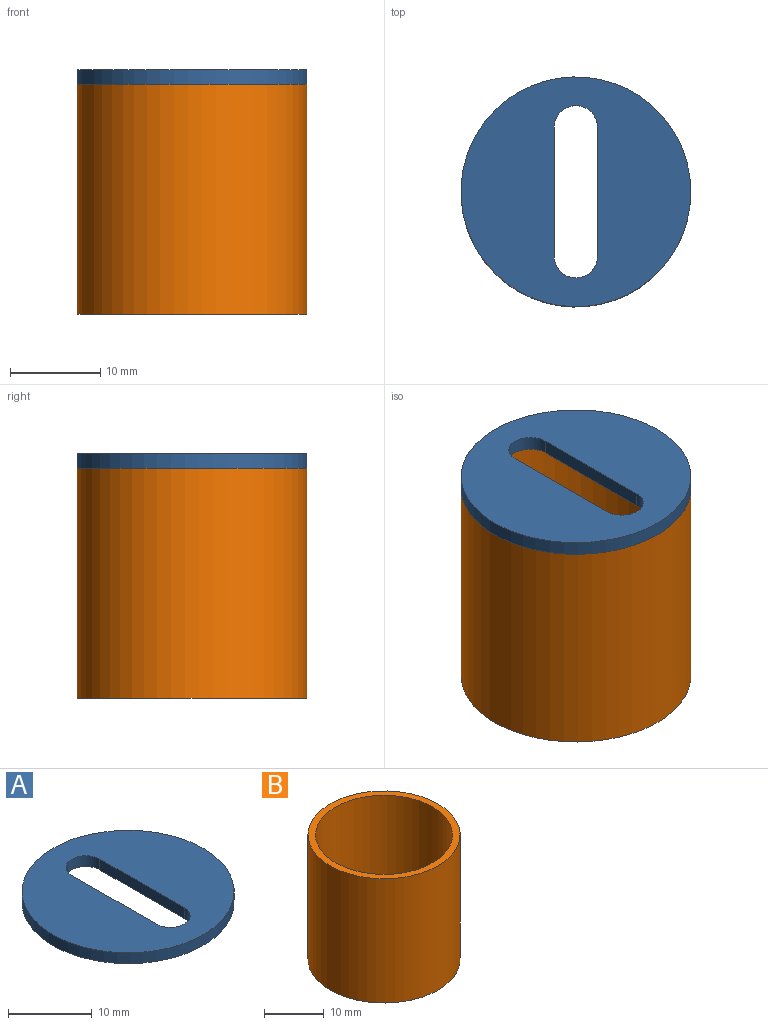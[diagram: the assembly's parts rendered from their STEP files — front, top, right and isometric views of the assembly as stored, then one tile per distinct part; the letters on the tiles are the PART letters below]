
ASSEMBLY  parts=2 mates=1
PART A: 7 faces, bbox 25.4x25.4x1.6 mm
  f0: cylinder r=2.38mm len=4.76mm, axis (0,0,-1), area 11.9mm2, adj f1,f3,f5,f6
  f1: plane 14.29x1.59mm, normal (-1,0,0), area 22.7mm2, adj f0,f2,f5,f6
  f2: cylinder r=2.38mm len=4.76mm, axis (0,0,-1), area 11.9mm2, adj f1,f3,f5,f6
  f3: plane 14.29x1.59mm, normal (1,0,0), area 22.7mm2, adj f0,f2,f5,f6
  f4: cylinder r=12.7mm len=25.4mm, axis (0,0,-1), area 126.7mm2, adj f5,f6
  f5: plane 25.4x25.4mm, normal (0,0,1), area 420.8mm2, adj f0,f1,f2,f3,f4
  f6: plane 25.4x25.4mm, normal (0,0,-1), area 420.8mm2, adj f0,f1,f2,f3,f4
PART B: 4 faces, bbox 25.4x25.4x25.4 mm
  f0: cylinder r=11.43mm len=25.4mm, axis (0,0,-1), area 1824.1mm2, adj f2,f3
  f1: cylinder r=12.7mm len=25.4mm, axis (0,0,-1), area 2026.8mm2, adj f2,f3
  f2: plane 25.4x25.4mm, normal (0,0,1), area 96.3mm2, adj f0,f1
  f3: plane 25.4x25.4mm, normal (0,0,-1), area 96.3mm2, adj f0,f1
PLACE A rot(axis=(1,0,0),180deg) t=(0,0,26.99)mm
PLACE B at identity
MATE fastened A.f4 <-> B.f1  axis (0,0,-1) through (0,0,25.4)mm
